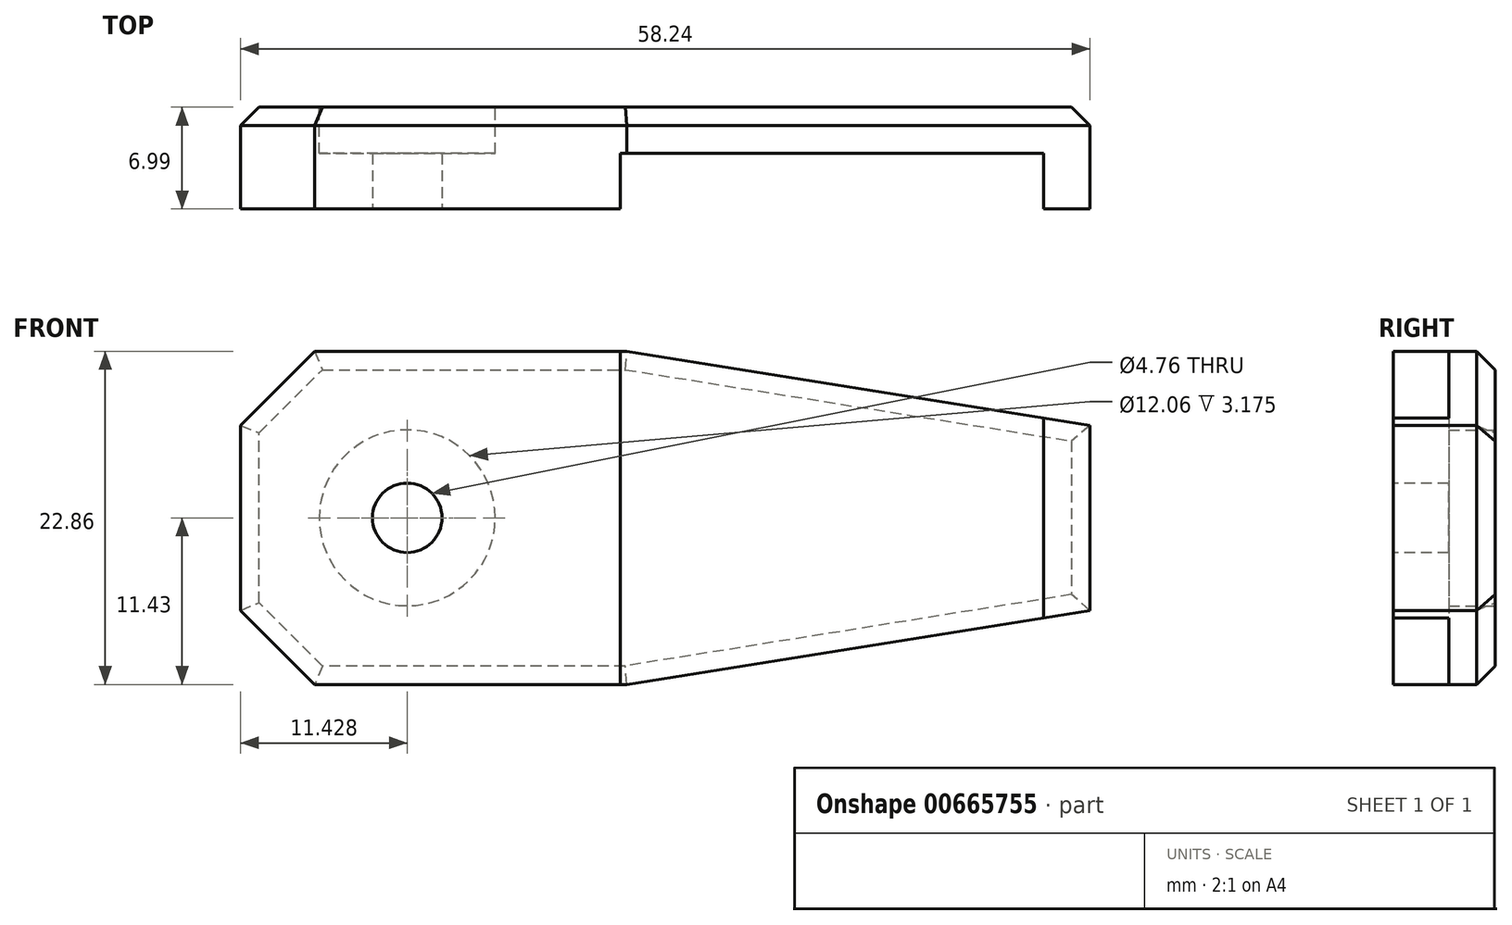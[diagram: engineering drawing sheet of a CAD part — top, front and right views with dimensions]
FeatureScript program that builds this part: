
annotation { "Feature Type Name" : "Feature", "Feature Type Description" : "" }
export const myFeature = defineFeature(function(context is Context, id is Id, definition is map)
    precondition{}
    {
        {
            var Q0;
            Q0=qCreatedBy(makeId("Top.planeOp"),FACE);
            var sketch = newSketch(context, id + "F0", { "sketchPlane" : qUnion([Q0])});
            skLineSegment(sketch, "E0", {"start": v(-6.6, 0) * mm, "end": v(-6.6, 3.18) * mm});
            skLineSegment(sketch, "E1", {"start": v(-6.6, 3.18) * mm, "end": v(16.27, 3.18) * mm});
            skLineSegment(sketch, "E2", {"start": v(-6.6, 0) * mm, "end": v(19.44, 0) * mm});
            skLineSegment(sketch, "E3", {"start": v(19.44, 0) * mm, "end": v(19.44, 3.81) * mm});
            skLineSegment(sketch, "E4", {"start": v(19.44, 3.81) * mm, "end": v(48.47, 3.81) * mm});
            skLineSegment(sketch, "E5", {"start": v(48.47, 3.81) * mm, "end": v(48.47, 0) * mm});
            skLineSegment(sketch, "E6", {"start": v(48.47, 0) * mm, "end": v(51.65, 0) * mm});
            skLineSegment(sketch, "E7", {"start": v(51.65, 6.99) * mm, "end": v(51.65, 0) * mm});
            skLineSegment(sketch, "E8", {"start": v(51.65, 6.99) * mm, "end": v(16.27, 6.98) * mm});
            skLineSegment(sketch, "E9", {"start": v(16.27, 6.98) * mm, "end": v(16.27, 3.17) * mm});
            skSolve(sketch);
        }
        {
            var Q0;
            Q0=makeQuery(id+"F0.imprint","IMPRINT",FACE,{"disambiguationData":[TD([[makeQuery(id+"F0.imprint","IMPRINT",EDGE,{"derivedFrom":sQuery(id+"F0.wireOp",EDGE,"E0")}),-1.0]])]});
            extrude(context, id + "F1", {"entities" : qUnion([Q0]), "depth" : 22.86 * mm, "offsetDistance" : 25.4 * mm});
        }
        {
            var Q0;
            Q0=makeQuery(id+"F1.opExtrude","CAP_EDGE",EDGE,{"disambiguationData":[OSD([sQuery(id+"F0.wireOp",EDGE,"E7")])],"isStart":false});
            var Q1;
            Q1=makeQuery(id+"F1.opExtrude","CAP_EDGE",EDGE,{"disambiguationData":[OSD([sQuery(id+"F0.wireOp",EDGE,"E7")])],"isStart":true});
            chamfer(context, id + "F2", {"entities" : qUnion([Q0, Q1]), "chamferType" : ChamferType.TWO_OFFSETS, "width1" : 5.08 * mm, "oppositeDirection" : false, "width2" : 31.75 * mm, "tangentPropagation" : true});
        }
        {
            var Q0;
            Q0=makeQuery(id+"F1.opExtrude","CAP_EDGE",EDGE,{"disambiguationData":[OSD([sQuery(id+"F0.wireOp",EDGE,"E0")])],"isStart":true});
            var Q1;
            Q1=makeQuery(id+"F1.opExtrude","CAP_EDGE",EDGE,{"disambiguationData":[OSD([sQuery(id+"F0.wireOp",EDGE,"E0")])],"isStart":false});
            chamfer(context, id + "F3", {"entities" : qUnion([Q0, Q1]), "width" : 5.08 * mm, "tangentPropagation" : true});
        }
        {
            var Q0;
            Q0=makeQuery(id+"F1.opExtrude","SWEPT_FACE",FACE,{"disambiguationData":[OSD([sQuery(id+"F0.wireOp",EDGE,"E1")])]});
            var sketch = newSketch(context, id + "F4", { "sketchPlane" : qUnion([Q0])});
            skLineSegment(sketch, "E10.0.0", {"start": v(6.6, 5.08) * mm, "end": v(6.6, 17.78) * mm});
            skLineSegment(sketch, "E10.0.1", {"start": v(6.6, 17.78) * mm, "end": v(1.51, 22.86) * mm});
            skLineSegment(sketch, "E10.0.2", {"start": v(1.51, 22.86) * mm, "end": v(-16.27, 22.86) * mm});
            skLineSegment(sketch, "E10.0.3", {"start": v(-16.27, 22.86) * mm, "end": v(-16.27, 0) * mm});
            skLineSegment(sketch, "E10.0.4", {"start": v(-16.27, 0) * mm, "end": v(1.51, 0) * mm});
            skLineSegment(sketch, "E10.0.5", {"start": v(1.51, 0) * mm, "end": v(6.6, 5.08) * mm});
            skSolve(sketch);
        }
        {
            var Q0;
            Q0 = qSketchRegion(id + "F4", true);
            var Q1;
            Q1=makeQuery(id+"F1.opExtrude","SWEPT_FACE",FACE,{"disambiguationData":[OSD([sQuery(id+"F0.wireOp",EDGE,"E8")])]});
            extrude(context, id + "F5", {"entities" : qUnion([Q0]), "operationType" : NewBodyOperationType.ADD, "endBound" : BoundingType.UP_TO_SURFACE, "depth" : 25.4 * mm, "endBoundEntityFace" : qUnion([Q1]), "offsetDistance" : 25.4 * mm});
        }
        {
            var Q0;
            {var subQ0=sQuery(id+"F0.wireOp",EDGE,"E8");Q0=makeQuery(id+"F5.boolean.opBoolean","MERGE",FACE,{"derivedFrom":[makeQuery(id+"F1.opExtrude","SWEPT_FACE",FACE,{"disambiguationData":[OSD([subQ0])]}),makeQuery(id+"F5.opExtrude","CAP_FACE",FACE,{"disambiguationData":[OSD([subQ0])],"isStart":false})]});}
            chamfer(context, id + "F6", {"entities" : qUnion([Q0]), "width" : 1.27 * mm, "tangentPropagation" : true});
        }
        {
            var Q0;
            Q0=makeQuery(id+"F1.opExtrude","SWEPT_FACE",FACE,{"disambiguationData":[OSD([sQuery(id+"F0.wireOp",EDGE,"E2")])]});
            var sketch = newSketch(context, id + "F7", { "sketchPlane" : qUnion([Q0])});
            skCircle(sketch, "E11", {"center": v(4.84, 11.43) * mm, "radius": 2.38 * mm});
            skSolve(sketch);
        }
        {
            var Q0;
            Q0 = qSketchRegion(id + "F7", true);
            extrude(context, id + "F8", {"entities" : qUnion([Q0]), "operationType" : NewBodyOperationType.REMOVE, "oppositeDirection" : true, "depth" : 25.4 * mm, "offsetDistance" : 25.4 * mm});
        }
        {
            var Q0;
            {var subQ0=sQuery(id+"F0.wireOp",EDGE,"E8");Q0=makeQuery(id+"F5.boolean.opBoolean","MERGE",FACE,{"derivedFrom":[makeQuery(id+"F1.opExtrude","SWEPT_FACE",FACE,{"disambiguationData":[OSD([subQ0])]}),makeQuery(id+"F5.opExtrude","CAP_FACE",FACE,{"disambiguationData":[OSD([subQ0])],"isStart":false})]});}
            var sketch = newSketch(context, id + "F9", { "sketchPlane" : qUnion([Q0])});
            skCircle(sketch, "E12.0", {"center": v(-4.84, 11.43) * mm, "radius": 2.38 * mm});
            skCircle(sketch, "E13", {"center": v(-4.84, 11.43) * mm, "radius": 6.03 * mm});
            skSolve(sketch);
        }
        {
            var Q0;
            Q0=makeQuery(id+"F9.imprint","IMPRINT",FACE,{"disambiguationData":[TD([[makeQuery(id+"F9.imprint","IMPRINT",EDGE,{"derivedFrom":sQuery(id+"F9.wireOp",EDGE,"E12.0")}),1.0]])]});
            extrude(context, id + "F10", {"entities" : qUnion([Q0]), "operationType" : NewBodyOperationType.REMOVE, "oppositeDirection" : true, "depth" : 3.17 * mm, "offsetDistance" : 25.4 * mm});
        }
    });
